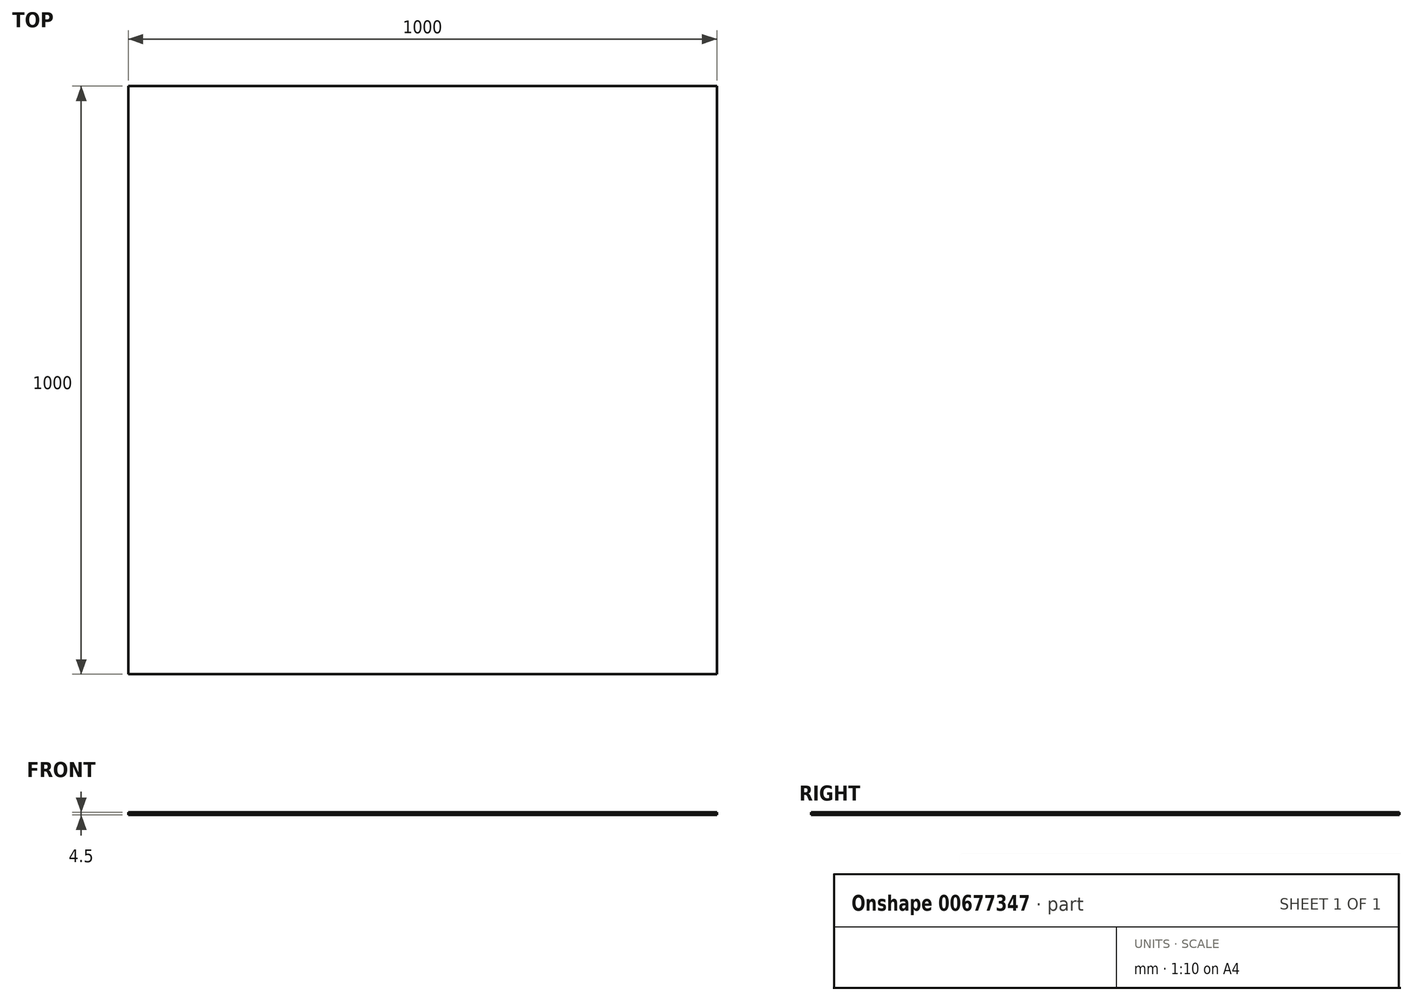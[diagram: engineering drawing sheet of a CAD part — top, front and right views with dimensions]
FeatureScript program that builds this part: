
annotation { "Feature Type Name" : "Feature", "Feature Type Description" : "" }
export const myFeature = defineFeature(function(context is Context, id is Id, definition is map)
    precondition{}
    {
        {
            var Q0;
            Q0=qCreatedBy(makeId("Top.planeOp"),FACE);
            var sketch = newSketch(context, id + "F0", { "sketchPlane" : qUnion([Q0])});
            skLineSegment(sketch, "E0.bottom", {"start": v(-500, 500) * mm, "end": v(500, 500) * mm});
            skLineSegment(sketch, "E0.top", {"start": v(-500, -500) * mm, "end": v(500, -500) * mm});
            skLineSegment(sketch, "E0.left", {"start": v(-500, 500) * mm, "end": v(-500, -500) * mm});
            skLineSegment(sketch, "E0.right", {"start": v(500, 500) * mm, "end": v(500, -500) * mm});
            skPoint(sketch, "E0.middle", {"position": v(0, 0) * mm});
            skSolve(sketch);
        }
        {
            var Q0;
            Q0=makeQuery(id+"F0.imprint","IMPRINT",FACE,{"disambiguationData":[TD([[makeQuery(id+"F0.imprint","IMPRINT",EDGE,{"derivedFrom":sQuery(id+"F0.wireOp",EDGE,"4Ersnz3Q-Dc8a-a7wz-1zxC-W19j0GPysHq9.bottom")}),1.0]])]});
            var Q1;
            Q1=makeQuery(id+"F0.imprint","IMPRINT",FACE,{"disambiguationData":[TD([[makeQuery(id+"F0.imprint","IMPRINT",EDGE,{"derivedFrom":sQuery(id+"F0.wireOp",EDGE,"4Ersnz3Q-Dc8a-a7wz-1zxC-W19j0GPysHq9.bottom")}),-1.0]])]});
            var Q2;
            Q2=makeQuery(id+"F0.imprint","IMPRINT",FACE,{"disambiguationData":[TD([[makeQuery(id+"F0.imprint","IMPRINT",EDGE,{"derivedFrom":sQuery(id+"F0.wireOp",EDGE,"E0.bottom")}),-1.0]])]});
            extrude(context, id + "F1", {"entities" : qUnion([Q0, Q1, Q2]), "depth" : 4.5 * mm, "offsetDistance" : 25 * mm});
        }
    });
